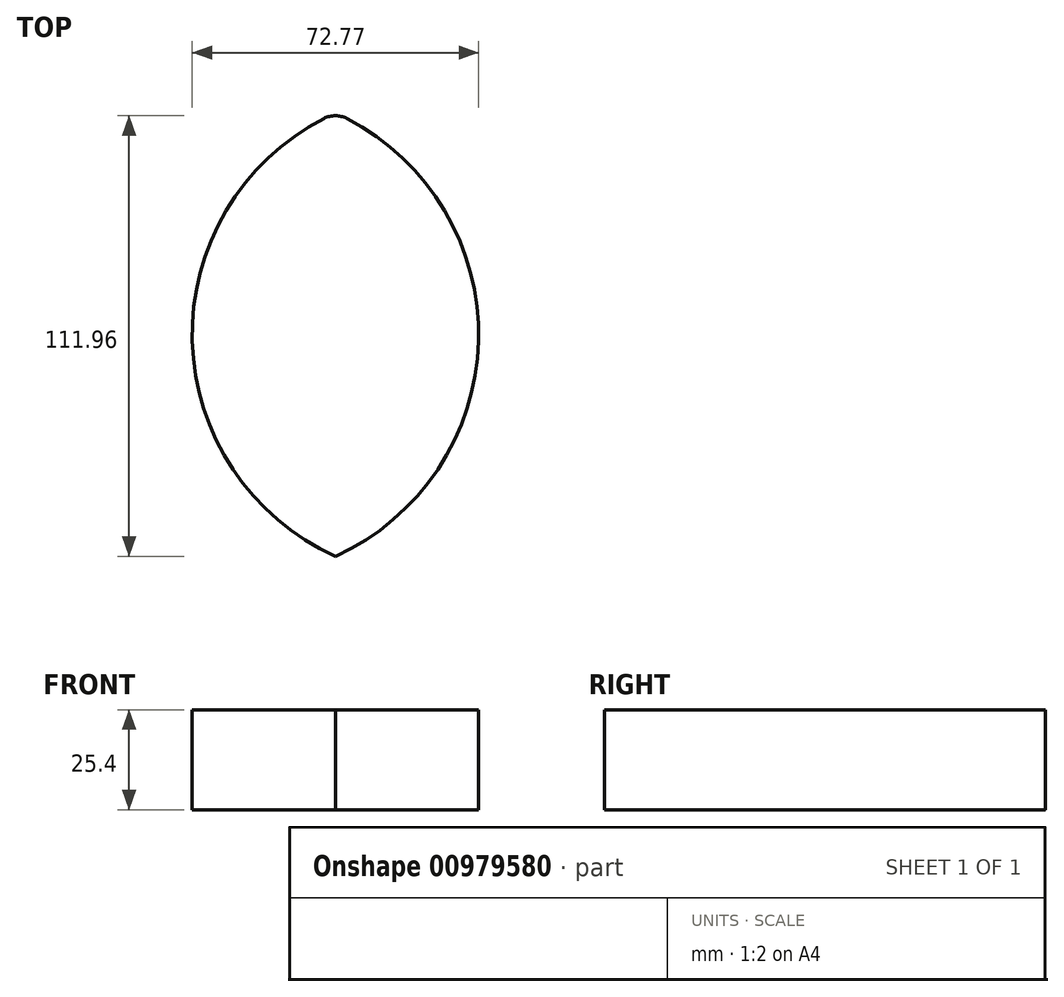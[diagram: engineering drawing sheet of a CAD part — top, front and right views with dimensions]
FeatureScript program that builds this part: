
annotation { "Feature Type Name" : "Feature", "Feature Type Description" : "" }
export const myFeature = defineFeature(function(context is Context, id is Id, definition is map)
    precondition{}
    {
        {
            var Q0;
            Q0=qCreatedBy(makeId("Top.planeOp"),FACE);
            var sketch = newSketch(context, id + "F0", { "sketchPlane" : qUnion([Q0])});
            skArc(sketch, "E0", {"start": v(0, -56.53) * mm, "mid": v(36.37, -1.82) * mm, "end": v(2.91, 54.72) * mm});
            skArc(sketch, "E1", {"start": v(-2.91, 54.72) * mm, "mid": v(-36.36, -1.82) * mm, "end": v(0, -56.53) * mm});
            skPoint(sketch, "E2.visualSharp", {"position": v(0, 56.13) * mm});
            skArc(sketch, "E2.filletArc", {"start": v(2.91, 54.72) * mm, "mid": v(0, 55.43) * mm, "end": v(-2.91, 54.72) * mm});
            skSolve(sketch);
        }
        {
            var Q0;
            Q0 = qSketchRegion(id + "F0", true);
            extrude(context, id + "F1", {"entities" : qUnion([Q0]), "depth" : 25.4 * mm, "offsetDistance" : 25.4 * mm});
        }
    });
